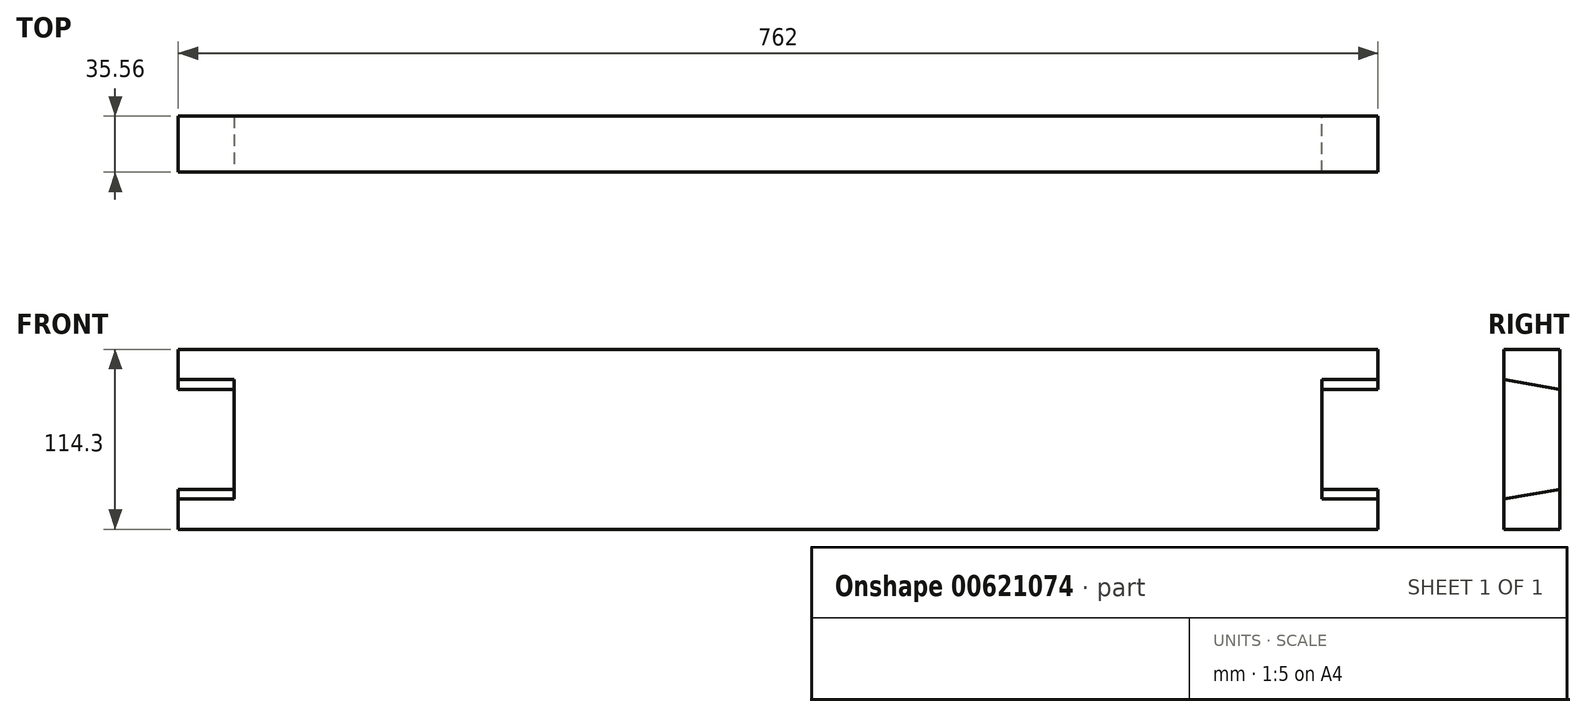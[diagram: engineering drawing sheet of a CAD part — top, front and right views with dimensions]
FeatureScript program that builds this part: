
annotation { "Feature Type Name" : "Feature", "Feature Type Description" : "" }
export const myFeature = defineFeature(function(context is Context, id is Id, definition is map)
    precondition{}
    {
        {
            var Q0;
            Q0=qCreatedBy(makeId("Front.planeOp"),FACE);
            var sketch = newSketch(context, id + "F0", { "sketchPlane" : qUnion([Q0])});
            skLineSegment(sketch, "E0.bottom", {"start": v(-381, 57.15) * mm, "end": v(381, 57.15) * mm});
            skLineSegment(sketch, "E0.top", {"start": v(-381, -57.15) * mm, "end": v(381, -57.15) * mm});
            skLineSegment(sketch, "E0.left", {"start": v(-381, 57.15) * mm, "end": v(-381, -57.15) * mm});
            skLineSegment(sketch, "E0.right", {"start": v(381, 57.15) * mm, "end": v(381, -57.15) * mm});
            skSolve(sketch);
        }
        {
            var Q0;
            Q0 = qSketchRegion(id + "F0", true);
            extrude(context, id + "F1", {"entities" : qUnion([Q0]), "depth" : 35.56 * mm, "offsetDistance" : 25.4 * mm});
        }
        {
            var Q0;
            Q0=makeQuery(id+"F1.opExtrude","SWEPT_FACE",FACE,{"disambiguationData":[OSD([sQuery(id+"F0.wireOp",EDGE,"E0.left")])]});
            var sketch = newSketch(context, id + "F2", { "sketchPlane" : qUnion([Q0])});
            skLineSegment(sketch, "E1", {"start": v(0, 31.75) * mm, "end": v(35.56, 38.02) * mm});
            skLineSegment(sketch, "E2", {"start": v(35.56, 38.02) * mm, "end": v(35.56, -38.02) * mm});
            skLineSegment(sketch, "E3", {"start": v(35.56, -38.02) * mm, "end": v(0, -31.75) * mm});
            skLineSegment(sketch, "E4", {"start": v(0, -31.75) * mm, "end": v(0, 31.75) * mm});
            skSolve(sketch);
        }
        {
            var Q0;
            Q0 = qSketchRegion(id + "F2", true);
            extrude(context, id + "F3", {"entities" : qUnion([Q0]), "operationType" : NewBodyOperationType.REMOVE, "oppositeDirection" : true, "depth" : 35.56 * mm, "offsetDistance" : 25.4 * mm});
        }
        {
            var Q0;
            Q0=makeQuery(id+"F1.opExtrude","SWEPT_FACE",FACE,{"disambiguationData":[OSD([sQuery(id+"F0.wireOp",EDGE,"E0.right")])]});
            var sketch = newSketch(context, id + "F4", { "sketchPlane" : qUnion([Q0])});
            skLineSegment(sketch, "E5", {"start": v(-35.56, 38.02) * mm, "end": v(0, 31.75) * mm});
            skLineSegment(sketch, "E6", {"start": v(0, 31.75) * mm, "end": v(0, -31.75) * mm});
            skLineSegment(sketch, "E7", {"start": v(0, -31.75) * mm, "end": v(-35.56, -38.02) * mm});
            skLineSegment(sketch, "E8", {"start": v(-35.56, -38.02) * mm, "end": v(-35.56, 38.02) * mm});
            skSolve(sketch);
        }
        {
            var Q0;
            Q0 = qSketchRegion(id + "F4", true);
            extrude(context, id + "F5", {"entities" : qUnion([Q0]), "operationType" : NewBodyOperationType.REMOVE, "oppositeDirection" : true, "depth" : 35.56 * mm, "offsetDistance" : 25.4 * mm});
        }
    });
